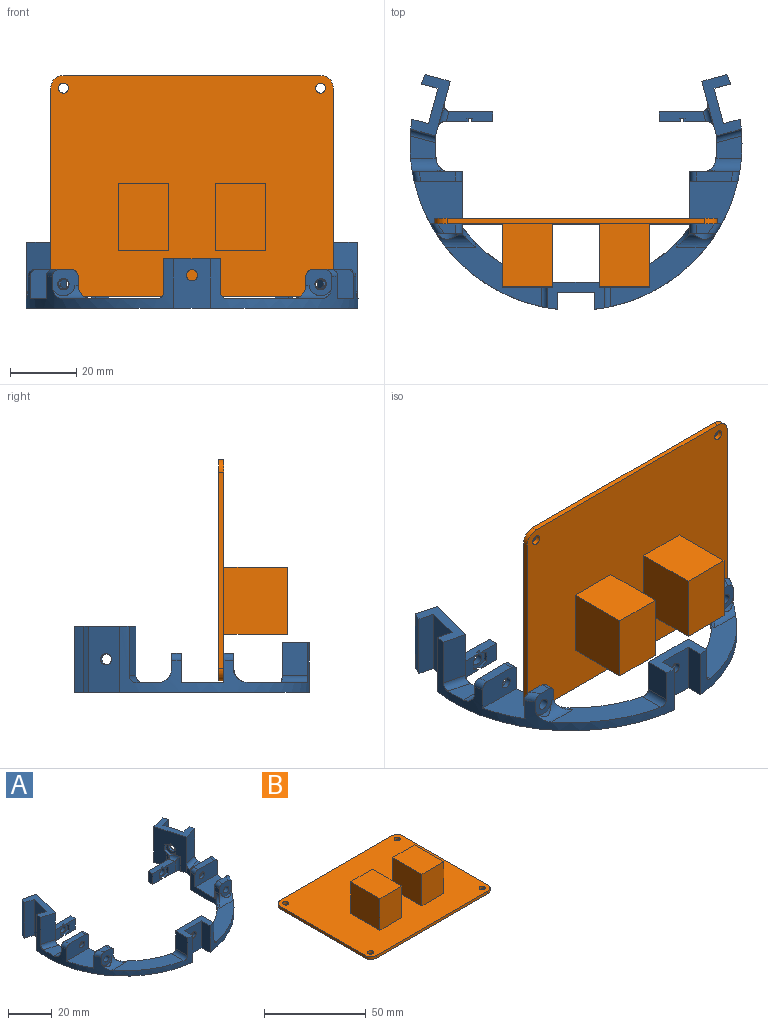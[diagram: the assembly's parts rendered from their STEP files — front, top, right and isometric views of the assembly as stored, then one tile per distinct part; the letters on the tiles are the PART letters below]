
ASSEMBLY  parts=2 mates=1
PART A: 148 faces, bbox 100.8x70.8x20.2 mm
  f0: plane 17x15mm, normal (0,1,0), area 226.7mm2, adj f1,f2,f28,f39,f41,f95,f96,f97
  f1: plane 10x7.77mm, normal (-1,0,0), area 77.7mm2, adj f0,f3,f127,f147
  f2: plane 10x7.77mm, normal (1,0,0), area 77.7mm2, adj f0,f4,f129,f147
  f3: cylinder r=50mm len=57.25mm, axis (0,0,-1), area 383.3mm2, adj f1,f5,f10,f27,f28,f29,f30,f35
  f4: cylinder r=50mm len=57.25mm, axis (0,0,-1), area 383.3mm2, adj f2,f7,f11,f23,f24,f28,f42,f43
  f5: plane 15x5.2mm, normal (1,0,0), area 77.9mm2, adj f3,f6,f28,f147
  f6: plane 15x11mm, normal (0,-1,0), area 155.9mm2, adj f5,f7,f22,f28,f147
  f7: plane 15x5.2mm, normal (-1,0,0), area 77.9mm2, adj f4,f6,f28,f147
  f8: cylinder r=1.7mm len=3.4mm, axis (0,1,0), area 32mm2, adj f43,f58
  f9: cylinder r=1.7mm len=3.4mm, axis (0,1,0), area 32mm2, adj f38,f60
  f10: cylinder r=4mm len=11.73mm, axis (1,0,0), area 33mm2, adj f3,f40,f60,f77,f146
  f11: cylinder r=4mm len=11.73mm, axis (1,0,0), area 33mm2, adj f4,f42,f43,f78,f145
  f12: plane 6.48x6mm, normal (0,-1,0), area 28mm2, adj f13,f28,f116,f132,f133,f134
  f13: plane 14.07x3.07mm, normal (0,0,1), area 40mm2, adj f12,f116,f117,f118,f124,f125,f134,f135
  f14: plane 7.09x6.07mm, normal (0,-1,0), area 31.7mm2, adj f16,f28,f122,f123,f138,f139,f140
  f15: plane 6.48x6mm, normal (0,-1,0), area 28mm2, adj f16,f28,f120,f141,f142,f143
  f16: plane 14.07x3.07mm, normal (0,0,1), area 40mm2, adj f14,f15,f119,f120,f121,f122,f140,f141
  f17: cylinder r=1.7mm len=3.4mm, axis (0,-1,0), area 21.4mm2, adj f119,f144
  f18: cylinder r=1.7mm len=3.4mm, axis (0,-1,0), area 21.4mm2, adj f117,f137
  f19: plane 20x16.42mm, normal (0.97,-0.26,0), area 256.5mm2, adj f26,f28,f29,f31,f35,f102,f103,f104
  f20: cylinder r=1.7mm len=3.67mm, axis (-0.97,-0.26,0), area 16mm2, adj f55,f115
  f21: cylinder r=1.7mm len=3.67mm, axis (0.97,-0.26,0), area 16mm2, adj f34,f108
  f22: cylinder r=1.7mm len=3.4mm, axis (0,1,0), area 16mm2, adj f6,f101
  f23: plane 15.18x11.9mm, normal (0,1,0), area 76.2mm2, adj f4,f24,f25,f28,f44,f57,f73,f74
  f24: cylinder r=4mm len=9.58mm, axis (-1,0,0), area 51.2mm2, adj f4,f23,f25,f47,f48,f88,f93
  f25: cylinder r=4mm len=4.88mm, axis (0,0,-1), area 23.2mm2, adj f23,f24,f28,f47,f88,f89
  f26: cylinder r=42.36mm len=7.17mm, axis (0,0,-1), area 22.4mm2, adj f19,f27,f28,f79,f80,f130
  f27: plane 7.85x6.71mm, normal (0,0,1), area 43.6mm2, adj f3,f26,f79,f130
  f28: plane 100x70.66mm, normal (0,0,-1), area 1521.3mm2, adj f0,f3,f4,f5,f6,f7,f12,f14
  f29: plane 15x7.51mm, normal (-0.26,-0.97,0), area 116.6mm2, adj f3,f19,f35,f130
  f30: plane 20x5.02mm, normal (0.26,0.97,0), area 103.9mm2, adj f3,f28,f34,f35
  f31: plane 20x7.51mm, normal (0.26,0.97,0), area 155.4mm2, adj f19,f28,f32,f35
  f32: cylinder r=50mm len=20mm, axis (0,0,-1), area 60.6mm2, adj f28,f31,f33,f35
  f33: plane 20x5.02mm, normal (-0.26,-0.97,0), area 103.9mm2, adj f28,f32,f34,f35
  f34: plane 20x10.63mm, normal (-0.97,0.26,0), area 210.9mm2, adj f21,f28,f30,f33,f35
  f35: plane 18.43x11.91mm, normal (0,0,1), area 81mm2, adj f3,f19,f29,f30,f31,f32,f33,f34
  f36: plane 18.8x9.76mm, normal (1,0,0), area 77.4mm2, adj f28,f37,f38,f60,f62,f63,f68,f69
  f37: plane 14.44x12.8mm, normal (0,0,1), area 158mm2, adj f3,f36,f38,f62
  f38: plane 9.57x8.76mm, normal (0,1,0), area 72.9mm2, adj f3,f9,f36,f37,f61,f67,f68
  f39: cylinder r=42.36mm len=25.39mm, axis (0,0,-1), area 96.7mm2, adj f0,f28,f40,f75,f77,f127
  f40: plane 28.73x19.27mm, normal (0,0,1), area 214.2mm2, adj f3,f10,f39,f77,f127
  f41: cylinder r=42.36mm len=25.39mm, axis (0,0,-1), area 96.7mm2, adj f0,f28,f42,f76,f78,f129
  f42: plane 28.73x19.27mm, normal (0,0,1), area 214.2mm2, adj f4,f11,f41,f78,f129
  f43: plane 7.95x7.79mm, normal (0,-1,0), area 43.1mm2, adj f4,f8,f11,f44,f59,f71,f72,f145
  f44: plane 18.8x9.76mm, normal (-1,0,0), area 77.4mm2, adj f23,f28,f43,f45,f46,f58,f71,f73
  f45: plane 14.44x12.8mm, normal (0,0,1), area 158mm2, adj f4,f44,f46,f58
  f46: plane 14.44x8.76mm, normal (0,-1,0), area 115.6mm2, adj f4,f44,f45,f57,f66,f73,f74
  f47: cylinder r=42.36mm len=7.17mm, axis (0,0,-1), area 22.4mm2, adj f24,f25,f28,f48,f53,f128
  f48: plane 7.85x6.71mm, normal (0,0,1), area 43.6mm2, adj f4,f24,f47,f128
  f49: plane 15x7.51mm, normal (0.26,-0.97,0), area 116.6mm2, adj f4,f53,f56,f128
  f50: plane 20x5.02mm, normal (0.26,-0.97,0), area 103.9mm2, adj f28,f51,f55,f56
  f51: cylinder r=50mm len=20mm, axis (0,0,-1), area 60.6mm2, adj f28,f50,f52,f56
  f52: plane 20x7.51mm, normal (-0.26,0.97,0), area 155.4mm2, adj f28,f51,f53,f56
  f53: plane 20x16.42mm, normal (-0.97,-0.26,0), area 256.5mm2, adj f28,f47,f49,f52,f56,f109,f110,f111
  f54: plane 20x5.02mm, normal (-0.26,0.97,0), area 103.9mm2, adj f4,f28,f55,f56
  f55: plane 20x10.63mm, normal (0.97,0.26,0), area 210.9mm2, adj f20,f28,f50,f54,f56
  f56: plane 18.43x11.91mm, normal (0,0,1), area 81mm2, adj f4,f49,f50,f51,f52,f53,f54,f55
  f57: plane 11x3mm, normal (0,0,1), area 32.1mm2, adj f23,f46,f73,f74
  f58: plane 9.57x8.76mm, normal (0,1,0), area 72.9mm2, adj f4,f8,f44,f45,f59,f71,f72
  f59: plane 5.28x3mm, normal (0,0,1), area 13.1mm2, adj f43,f58,f71,f72
  f60: plane 7.95x7.79mm, normal (0,-1,0), area 43.1mm2, adj f3,f9,f10,f36,f61,f67,f68,f146
  f61: plane 5.28x3mm, normal (0,0,1), area 13.1mm2, adj f38,f60,f67,f68
  f62: plane 14.44x8.76mm, normal (0,-1,0), area 115.6mm2, adj f3,f36,f37,f64,f65,f69,f70
  f63: plane 15.18x11.9mm, normal (0,1,0), area 76.2mm2, adj f3,f28,f36,f64,f69,f70,f79,f80
  f64: plane 11x3mm, normal (0,0,1), area 32.1mm2, adj f62,f63,f69,f70
  f65: cylinder r=1.7mm len=3.4mm, axis (0,1,0), area 16mm2, adj f62,f87
  f66: cylinder r=1.7mm len=3.4mm, axis (0,1,0), area 16mm2, adj f46,f94
  f67: torus R=48mm, axis (0,0,1), area 11mm2, adj f3,f38,f60,f61
  f68: cylinder r=2mm len=3mm, axis (0,-1,0), area 9.4mm2, adj f36,f38,f60,f61
  f69: cylinder r=2mm len=3mm, axis (0,-1,0), area 9.4mm2, adj f36,f62,f63,f64
  f70: torus R=48mm, axis (0,0,1), area 9.5mm2, adj f3,f62,f63,f64
  f71: cylinder r=2mm len=3mm, axis (0,1,0), area 9.4mm2, adj f43,f44,f58,f59
  f72: torus R=48mm, axis (0,0,1), area 11mm2, adj f4,f43,f58,f59
  f73: cylinder r=2mm len=3mm, axis (0,1,0), area 9.4mm2, adj f23,f44,f46,f57
  f74: torus R=48mm, axis (0,0,1), area 9.5mm2, adj f4,f23,f46,f57
  f75: cylinder r=2mm len=7mm, axis (0,0,-1), area 7.9mm2, adj f28,f36,f39,f77
  f76: cylinder r=2mm len=7mm, axis (0,0,-1), area 7.9mm2, adj f28,f41,f44,f78
  f77: cylinder r=4mm len=6.78mm, axis (0,1,0), area 11.5mm2, adj f10,f36,f39,f40,f75
  f78: cylinder r=4mm len=6.78mm, axis (0,-1,0), area 11.5mm2, adj f11,f41,f42,f44,f76
  f79: cylinder r=4mm len=9.58mm, axis (-1,0,0), area 51.2mm2, adj f3,f26,f27,f63,f80,f84,f86
  f80: cylinder r=4mm len=4.88mm, axis (0,0,-1), area 23.2mm2, adj f26,f28,f63,f79,f85,f86
  f81: plane 2.86x1.65mm, normal (-0.5,0,-0.87), area 5mm2, adj f63,f82,f83,f87
  f82: plane 3.3x1.5mm, normal (-1,0,0), area 5mm2, adj f63,f81,f85,f87
  f83: plane 2.86x1.65mm, normal (0.5,0,-0.87), area 5mm2, adj f63,f81,f84,f87
  f84: plane 3.3x1.73mm, normal (1,0,0), area 5.1mm2, adj f63,f79,f83,f86,f87
  f85: plane 2.86x1.65mm, normal (-0.5,0,0.87), area 5mm2, adj f63,f80,f82,f86,f87
  f86: plane 2.89x2.14mm, normal (0.5,0,0.87), area 6mm2, adj f79,f80,f84,f85,f87
  f87: plane 6.6x5.72mm, normal (0,1,0), area 19.2mm2, adj f65,f81,f82,f83,f84,f85,f86
  f88: plane 2.89x2.14mm, normal (-0.5,0,0.87), area 6mm2, adj f24,f25,f89,f93,f94
  f89: plane 2.86x1.65mm, normal (0.5,0,0.87), area 5mm2, adj f23,f25,f88,f90,f94
  f90: plane 3.3x1.5mm, normal (1,0,0), area 5mm2, adj f23,f89,f91,f94
  f91: plane 2.86x1.65mm, normal (0.5,0,-0.87), area 5mm2, adj f23,f90,f92,f94
  f92: plane 2.86x1.65mm, normal (-0.5,0,-0.87), area 5mm2, adj f23,f91,f93,f94
  f93: plane 3.3x1.73mm, normal (-1,0,0), area 5.1mm2, adj f23,f24,f88,f92,f94
  f94: plane 6.6x5.72mm, normal (0,1,0), area 19.2mm2, adj f66,f88,f89,f90,f91,f92,f93
  f95: plane 2.86x1.65mm, normal (0.5,0,-0.87), area 5mm2, adj f0,f96,f100,f101
  f96: plane 2.86x1.65mm, normal (-0.5,0,-0.87), area 5mm2, adj f0,f95,f97,f101
  f97: plane 3.3x1.5mm, normal (-1,0,0), area 5mm2, adj f0,f96,f98,f101
  f98: plane 2.86x1.65mm, normal (-0.5,0,0.87), area 5mm2, adj f0,f97,f99,f101
  f99: plane 2.86x1.65mm, normal (0.5,0,0.87), area 5mm2, adj f0,f98,f100,f101
  f100: plane 3.3x1.5mm, normal (1,0,0), area 5mm2, adj f0,f95,f99,f101
  f101: plane 6.6x5.72mm, normal (0,1,0), area 19.2mm2, adj f22,f95,f96,f97,f98,f99,f100
  f102: plane 3.3x2.8mm, normal (0.13,0.48,0.87), area 5.3mm2, adj f19,f103,f107,f108,f125
  f103: plane 3.31x2.22mm, normal (-0.13,-0.48,0.87), area 5.3mm2, adj f19,f102,f104,f108,f124,f125
  f104: plane 3.3x1.45mm, normal (-0.26,-0.97,0), area 5mm2, adj f19,f103,f105,f108
  f105: plane 3.15x2.19mm, normal (-0.13,-0.48,-0.87), area 5mm2, adj f19,f104,f106,f108
  f106: plane 3.15x2.19mm, normal (0.13,0.48,-0.87), area 5mm2, adj f19,f105,f107,f108
  f107: plane 3.3x1.45mm, normal (0.26,0.97,0), area 4.9mm2, adj f19,f102,f106,f108
  f108: plane 6.6x5.52mm, normal (0.97,-0.26,0), area 19.2mm2, adj f21,f102,f103,f104,f105,f106,f107
  f109: plane 3.3x2.8mm, normal (-0.13,0.48,0.87), area 5.3mm2, adj f53,f110,f114,f115,f122
  f110: plane 3.3x1.45mm, normal (-0.26,0.97,0), area 4.9mm2, adj f53,f109,f111,f115
  f111: plane 3.15x2.19mm, normal (-0.13,0.48,-0.87), area 4.9mm2, adj f53,f110,f112,f115
  f112: plane 3.15x2.19mm, normal (0.13,-0.48,-0.87), area 5mm2, adj f53,f111,f113,f115
  f113: plane 3.3x1.45mm, normal (0.26,-0.97,0), area 5mm2, adj f53,f112,f114,f115
  f114: plane 3.31x2.22mm, normal (0.13,-0.48,0.87), area 5.3mm2, adj f53,f109,f113,f115,f121,f122
  f115: plane 6.6x5.52mm, normal (-0.97,-0.26,0), area 19.2mm2, adj f20,f109,f110,f111,f112,f113,f114
  f116: plane 6x3mm, normal (1,0,0), area 18mm2, adj f12,f13,f28,f117
  f117: plane 12.73x6mm, normal (0,1,0), area 67.3mm2, adj f13,f18,f28,f116,f124
  f118: plane 7.09x6.07mm, normal (0,-1,0), area 31.7mm2, adj f13,f28,f125,f126,f131,f135,f136
  f119: plane 12.73x6mm, normal (0,1,0), area 67.3mm2, adj f16,f17,f28,f120,f121
  f120: plane 6x3mm, normal (-1,0,0), area 18mm2, adj f15,f16,f28,f119
  f121: cylinder r=2mm len=7.64mm, axis (0,0,-1), area 24.1mm2, adj f16,f28,f53,f114,f119,f122
  f122: cylinder r=2mm len=6.7mm, axis (0.26,-0.97,0), area 11.9mm2, adj f14,f16,f53,f109,f114,f121,f123
  f123: cylinder r=2mm len=8mm, axis (0,0,-1), area 18mm2, adj f14,f28,f53,f122
  f124: cylinder r=2mm len=7.64mm, axis (0,0,1), area 24.1mm2, adj f13,f19,f28,f103,f117,f125
  f125: cylinder r=2mm len=6.7mm, axis (0.26,0.97,0), area 11.9mm2, adj f13,f19,f102,f103,f118,f124,f126
  f126: cylinder r=2mm len=8mm, axis (0,0,1), area 18mm2, adj f19,f28,f118,f125
  f127: cylinder r=2mm len=8.23mm, axis (0,-1,0), area 24.3mm2, adj f1,f3,f39,f40
  f128: cylinder r=2mm len=8.47mm, axis (0.97,0.26,0), area 24.3mm2, adj f4,f47,f48,f49
  f129: cylinder r=2mm len=8.23mm, axis (0,1,0), area 24.3mm2, adj f2,f4,f41,f42
  f130: cylinder r=2mm len=8.47mm, axis (0.97,-0.26,0), area 24.3mm2, adj f3,f26,f27,f29
  f131: plane 2.34x1.35mm, normal (0.5,0,0.87), area 2.7mm2, adj f28,f118,f136,f137
  f132: plane 2.34x1.35mm, normal (-0.5,0,0.87), area 2.7mm2, adj f12,f28,f133,f137
  f133: plane 3.3x1mm, normal (-1,0,0), area 3.3mm2, adj f12,f132,f134,f137
  f134: plane 2.34x1.35mm, normal (-0.5,0,-0.87), area 2.7mm2, adj f12,f13,f133,f137
  f135: plane 2.34x1.35mm, normal (0.5,0,-0.87), area 2.7mm2, adj f13,f118,f136,f137
  f136: plane 3.3x1mm, normal (1,0,0), area 3.3mm2, adj f118,f131,f135,f137
  f137: plane 6x5.72mm, normal (0,-1,0), area 18.9mm2, adj f13,f18,f28,f131,f132,f133,f134,f135
  f138: plane 2.34x1.35mm, normal (-0.5,0,0.87), area 2.7mm2, adj f14,f28,f139,f144
  f139: plane 3.3x1mm, normal (-1,0,0), area 3.3mm2, adj f14,f138,f140,f144
  f140: plane 2.34x1.35mm, normal (-0.5,0,-0.87), area 2.7mm2, adj f14,f16,f139,f144
  f141: plane 2.34x1.35mm, normal (0.5,0,-0.87), area 2.7mm2, adj f15,f16,f142,f144
  f142: plane 3.3x1mm, normal (1,0,0), area 3.3mm2, adj f15,f141,f143,f144
  f143: plane 2.34x1.35mm, normal (0.5,0,0.87), area 2.7mm2, adj f15,f28,f142,f144
  f144: plane 6x5.72mm, normal (0,-1,0), area 18.9mm2, adj f16,f17,f28,f138,f139,f140,f141,f142
  f145: cylinder r=3.5mm len=6.83mm, axis (0,1,0), area 7.8mm2, adj f4,f11,f43
  f146: cylinder r=3.5mm len=6.83mm, axis (0,1,0), area 7.8mm2, adj f3,f10,f60
  f147: plane 17x8.2mm, normal (0,0,1), area 81mm2, adj f0,f1,f2,f3,f4,f5,f6,f7
PART B: 24 faces, bbox 85.1x66.7x20.6 mm
  f0: plane 85.09x66.68mm, normal (0,0,1), area 5013.3mm2, adj f1,f2,f3,f4,f5,f6,f7,f8
  f1: plane 59.06x1.6mm, normal (1,0,0), area 94.5mm2, adj f0,f2,f12,f13
  f2: cylinder r=3.81mm len=3.81mm, axis (0,0,-1), area 9.6mm2, adj f0,f1,f3,f13
  f3: plane 77.47x1.6mm, normal (0,1,0), area 124mm2, adj f0,f2,f4,f13
  f4: cylinder r=3.81mm len=3.81mm, axis (0,0,-1), area 9.6mm2, adj f0,f3,f5,f13
  f5: plane 59.06x1.6mm, normal (-1,0,0), area 94.5mm2, adj f0,f4,f6,f13
  f6: cylinder r=3.81mm len=3.81mm, axis (0,0,-1), area 9.6mm2, adj f0,f5,f7,f13
  f7: plane 77.47x1.6mm, normal (0,-1,0), area 124mm2, adj f0,f6,f12,f13
  f8: cylinder r=1.5mm len=3mm, axis (0,0,-1), area 15.1mm2, adj f0,f13
  f9: cylinder r=1.5mm len=3mm, axis (0,0,-1), area 15.1mm2, adj f0,f13
  f10: cylinder r=1.5mm len=3mm, axis (0,0,-1), area 15.1mm2, adj f0,f13
  f11: cylinder r=1.5mm len=3mm, axis (0,0,-1), area 15.1mm2, adj f0,f13
  f12: cylinder r=3.81mm len=3.81mm, axis (0,0,-1), area 9.6mm2, adj f0,f1,f7,f13
  f13: plane 85.09x66.68mm, normal (0,0,-1), area 5632.6mm2, adj f1,f2,f3,f4,f5,f6,f7,f8
  f14: plane 20.32x19mm, normal (-1,0,0), area 386.1mm2, adj f0,f15,f17,f18
  f15: plane 19x15.24mm, normal (0,-1,0), area 289.6mm2, adj f0,f14,f16,f18
  f16: plane 20.32x19mm, normal (1,0,0), area 386.1mm2, adj f0,f15,f17,f18
  f17: plane 19x15.24mm, normal (0,1,0), area 289.6mm2, adj f0,f14,f16,f18
  f18: plane 20.32x15.24mm, normal (0,0,1), area 309.7mm2, adj f14,f15,f16,f17
  f19: plane 20.32x19mm, normal (1,0,0), area 386.1mm2, adj f0,f20,f22,f23
  f20: plane 19x15.24mm, normal (0,1,0), area 289.6mm2, adj f0,f19,f21,f23
  f21: plane 20.32x19mm, normal (-1,0,0), area 386.1mm2, adj f0,f20,f22,f23
  f22: plane 19x15.24mm, normal (0,-1,0), area 289.6mm2, adj f0,f19,f21,f23
  f23: plane 20.32x15.24mm, normal (0,0,1), area 309.7mm2, adj f19,f20,f21,f22
PLACE A t=(-726.56,-294.32,-19.68)mm
PLACE B rot(axis=(1,0,0),90deg) t=(-19.11,-16.72,-16.18)mm
MATE fastened B.f10 <-> A.f8  axis (0,-1,0) through (62.17,-18.32,-12.37)mm
